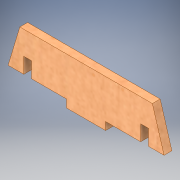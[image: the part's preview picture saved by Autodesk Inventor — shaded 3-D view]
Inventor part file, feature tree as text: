
AUTODESK INVENTOR PART (.ipt)
format: ipt  version: 2019 (Build 230136000, 136)  size: 127,488 bytes
history: native  units: mm
features: other x1, extrude x1, sketch x1
ambient origin geometry x8: Origin, YZ Plane, XZ Plane, XY Plane, X Axis, Y Axis, Z Axis, Center Point
bodies: Body1 (feature_tree)
feature tree (3):
  other  "Твердое тело1"
  extrude  "Выдавливание1"  Depth=4.0mm
  sketch  "Эскиз1"
